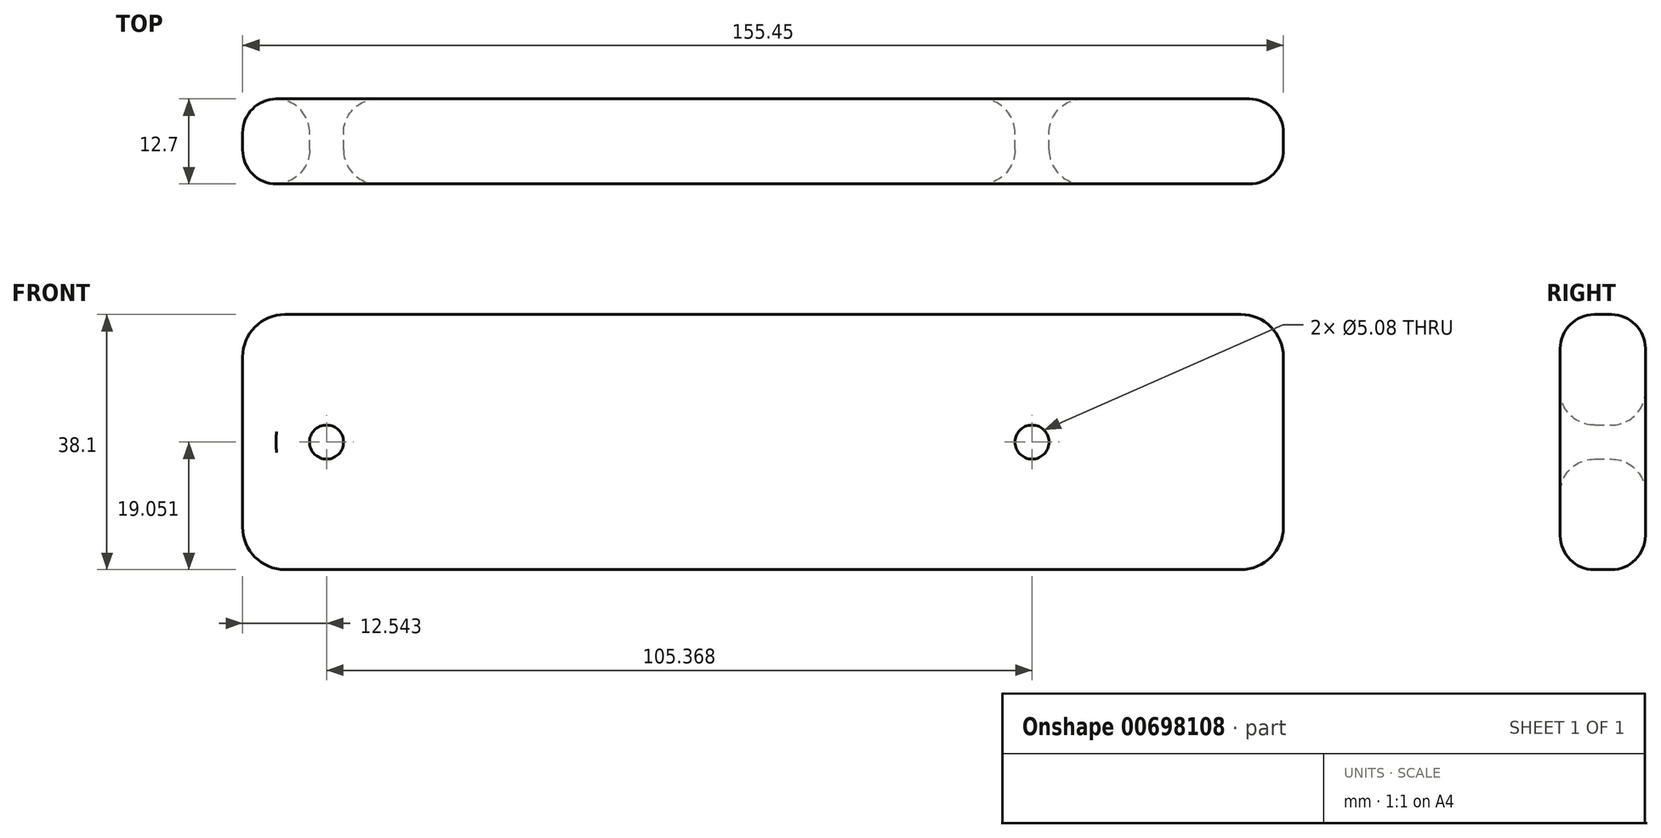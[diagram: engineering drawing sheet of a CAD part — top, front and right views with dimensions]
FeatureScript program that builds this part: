
annotation { "Feature Type Name" : "Feature", "Feature Type Description" : "" }
export const myFeature = defineFeature(function(context is Context, id is Id, definition is map)
    precondition{}
    {
        {
            var Q0;
            Q0=qCreatedBy(makeId("Front.planeOp"),FACE);
            var sketch = newSketch(context, id + "F0", { "sketchPlane" : qUnion([Q0])});
            skLineSegment(sketch, "E0.bottom", {"start": v(-71.76, 13.45) * mm, "end": v(71, 13.45) * mm});
            skLineSegment(sketch, "E0.top", {"start": v(-71.76, -24.65) * mm, "end": v(71, -24.65) * mm});
            skLineSegment(sketch, "E0.left", {"start": v(-78.1, 7.1) * mm, "end": v(-78.1, -18.3) * mm});
            skLineSegment(sketch, "E0.right", {"start": v(77.34, 7.1) * mm, "end": v(77.34, -18.3) * mm});
            skPoint(sketch, "E1.visualSharp", {"position": v(-78.1, 13.45) * mm});
            skArc(sketch, "E1.filletArc", {"start": v(-71.76, 13.45) * mm, "mid": v(-76.25, 11.6) * mm, "end": v(-78.1, 7.1) * mm});
            skPoint(sketch, "E2.visualSharp", {"position": v(77.34, 13.45) * mm});
            skArc(sketch, "E2.filletArc", {"start": v(77.34, 7.1) * mm, "mid": v(75.48, 11.6) * mm, "end": v(71, 13.45) * mm});
            skPoint(sketch, "E3.visualSharp", {"position": v(77.34, -24.65) * mm});
            skArc(sketch, "E3.filletArc", {"start": v(71, -24.65) * mm, "mid": v(75.48, -22.79) * mm, "end": v(77.34, -18.3) * mm});
            skPoint(sketch, "E4.visualSharp", {"position": v(-78.1, -24.65) * mm});
            skArc(sketch, "E4.filletArc", {"start": v(-78.1, -18.3) * mm, "mid": v(-76.25, -22.79) * mm, "end": v(-71.76, -24.65) * mm});
            skCircle(sketch, "E5", {"center": v(-65.57, -5.6) * mm, "radius": 2.54 * mm});
            skCircle(sketch, "E6", {"center": v(39.8, -5.6) * mm, "radius": 2.54 * mm});
            skSolve(sketch);
        }
        {
            var Q0;
            Q0 = qSketchRegion(id + "F0", true);
            extrude(context, id + "F1", {"entities" : qUnion([Q0]), "depth" : 12.7 * mm, "offsetDistance" : 25.4 * mm});
        }
        {
            var Q0;
            Q0=makeQuery(id+"F1.opExtrude","CAP_EDGE",EDGE,{"disambiguationData":[OSD([sQuery(id+"F0.wireOp",EDGE,"E0.bottom")])],"isStart":false});
            var Q1;
            Q1=makeQuery(id+"F1.opExtrude","CAP_EDGE",EDGE,{"disambiguationData":[OSD([sQuery(id+"F0.wireOp",EDGE,"E0.bottom")])],"isStart":true});
            var Q2;
            Q2=makeQuery(id+"F1.opExtrude","CAP_EDGE",EDGE,{"disambiguationData":[OSD([sQuery(id+"F0.wireOp",EDGE,"E0.top")])],"isStart":false});
            var Q3;
            Q3=makeQuery(id+"F1.opExtrude","CAP_FACE",FACE,{"disambiguationData":[OSD([sQuery(id+"F0.wireOp",EDGE,"E0.bottom"),sQuery(id+"F0.wireOp",EDGE,"E0.top"),sQuery(id+"F0.wireOp",EDGE,"E0.left"),sQuery(id+"F0.wireOp",EDGE,"E0.right"),sQuery(id+"F0.wireOp",EDGE,"E1.filletArc"),sQuery(id+"F0.wireOp",EDGE,"E2.filletArc"),sQuery(id+"F0.wireOp",EDGE,"E3.filletArc"),sQuery(id+"F0.wireOp",EDGE,"E4.filletArc"),sQuery(id+"F0.wireOp",EDGE,"E5"),sQuery(id+"F0.wireOp",EDGE,"E6")])],"isStart":true});
            var Q4;
            Q4=makeQuery(id+"F1.opExtrude","CAP_FACE",FACE,{"disambiguationData":[OSD([sQuery(id+"F0.wireOp",EDGE,"E0.bottom"),sQuery(id+"F0.wireOp",EDGE,"E0.top"),sQuery(id+"F0.wireOp",EDGE,"E0.left"),sQuery(id+"F0.wireOp",EDGE,"E0.right"),sQuery(id+"F0.wireOp",EDGE,"E1.filletArc"),sQuery(id+"F0.wireOp",EDGE,"E2.filletArc"),sQuery(id+"F0.wireOp",EDGE,"E3.filletArc"),sQuery(id+"F0.wireOp",EDGE,"E4.filletArc"),sQuery(id+"F0.wireOp",EDGE,"E5"),sQuery(id+"F0.wireOp",EDGE,"E6")])],"isStart":false});
            fillet(context, id + "F2", {"entities" : qUnion([Q0, Q1, Q2, Q3, Q4]), "radius" : 5.08 * mm, "tangentPropagation" : true, "allowEdgeOverflow" : false});
        }
    });
